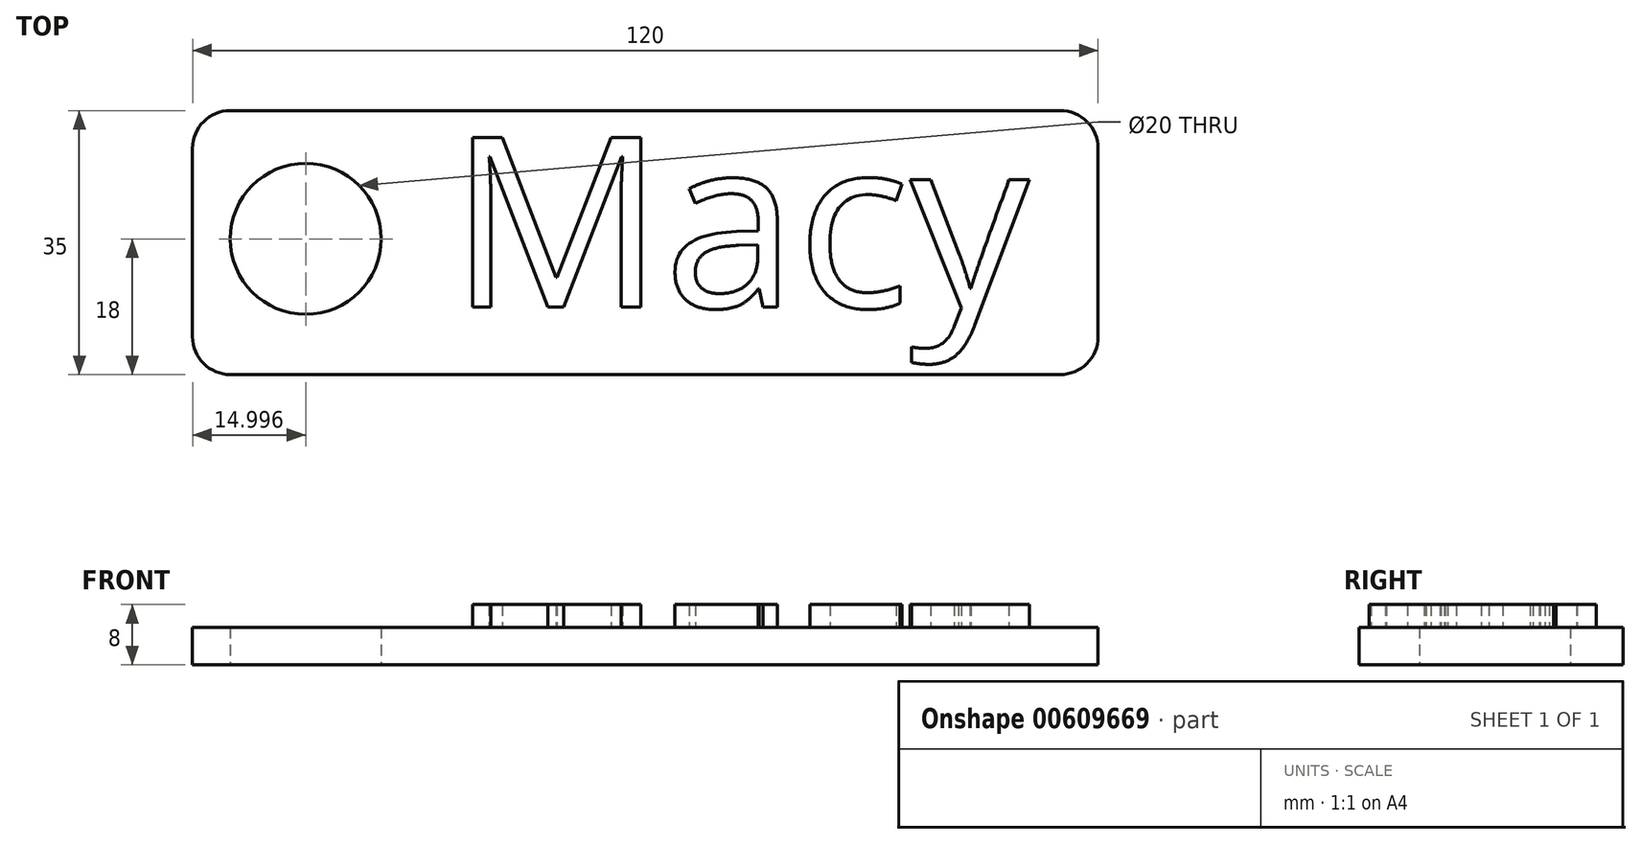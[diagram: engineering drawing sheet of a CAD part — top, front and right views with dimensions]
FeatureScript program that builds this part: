
annotation { "Feature Type Name" : "Feature", "Feature Type Description" : "" }
export const myFeature = defineFeature(function(context is Context, id is Id, definition is map)
    precondition{}
    {
        {
            var Q0;
            Q0=qCreatedBy(makeId("Top.planeOp"),FACE);
            var sketch = newSketch(context, id + "F0", { "sketchPlane" : qUnion([Q0])});
            skLineSegment(sketch, "E0.bottom", {"start": v(59.2, -18) * mm, "end": v(-60.8, -18) * mm});
            skLineSegment(sketch, "E0.top", {"start": v(59.2, 17) * mm, "end": v(-60.8, 17) * mm});
            skLineSegment(sketch, "E0.left", {"start": v(59.2, -18) * mm, "end": v(59.2, 17) * mm});
            skLineSegment(sketch, "E0.right", {"start": v(-60.8, -18) * mm, "end": v(-60.8, 17) * mm});
            skCircle(sketch, "E1", {"center": v(-45.8, 0) * mm, "radius": 10 * mm});
            skSolve(sketch);
        }
        {
            var Q0;
            Q0=makeQuery(id+"F0.imprint","IMPRINT",FACE,{"disambiguationData":[TD([[makeQuery(id+"F0.imprint","IMPRINT",EDGE,{"derivedFrom":sQuery(id+"F0.wireOp",EDGE,"E0.bottom")}),-1.0]])]});
            extrude(context, id + "F1", {"entities" : qUnion([Q0]), "depth" : 5 * mm, "offsetDistance" : 25 * mm});
        }
        {
            var Q0;
            Q0=makeQuery(id+"F1.opExtrude","CAP_FACE",FACE,{"disambiguationData":[OSD([sQuery(id+"F0.wireOp",EDGE,"E0.bottom"),sQuery(id+"F0.wireOp",EDGE,"E0.top"),sQuery(id+"F0.wireOp",EDGE,"E0.left"),sQuery(id+"F0.wireOp",EDGE,"E0.right"),sQuery(id+"F0.wireOp",EDGE,"E1")])],"isStart":false});
            var sketch = newSketch(context, id + "F2", { "sketchPlane" : qUnion([Q0])});
            skText(sketch, "E2", { "text": "Macy", "fontName": "OpenSans-Regular.ttf"});
            const initialGuessF2  = {"E2": [-0.0268, -0.00907, 1, 0, 0.02272]};
            skSetInitialGuess(sketch, initialGuessF2);
            skSolve(sketch);
        }
        {
            var Q0;
            Q0 = qSketchRegion(id + "F2", true);
            extrude(context, id + "F3", {"entities" : qUnion([Q0]), "operationType" : NewBodyOperationType.ADD, "depth" : 3 * mm, "offsetDistance" : 25 * mm});
        }
        {
            var Q0;
            Q0=makeQuery(id+"F1.opExtrude","SWEPT_EDGE",EDGE,{"disambiguationData":[OSD([sQuery(id+"F0.wireOp",EDGE,"E0.bottom"),sQuery(id+"F0.wireOp",EDGE,"E0.left")])]});
            var Q1;
            Q1=makeQuery(id+"F1.opExtrude","SWEPT_EDGE",EDGE,{"disambiguationData":[OSD([sQuery(id+"F0.wireOp",EDGE,"E0.top"),sQuery(id+"F0.wireOp",EDGE,"E0.left")])]});
            var Q2;
            Q2=makeQuery(id+"F1.opExtrude","SWEPT_EDGE",EDGE,{"disambiguationData":[OSD([sQuery(id+"F0.wireOp",EDGE,"E0.bottom"),sQuery(id+"F0.wireOp",EDGE,"E0.right")])]});
            var Q3;
            Q3=makeQuery(id+"F1.opExtrude","SWEPT_EDGE",EDGE,{"disambiguationData":[OSD([sQuery(id+"F0.wireOp",EDGE,"E0.top"),sQuery(id+"F0.wireOp",EDGE,"E0.right")])]});
            fillet(context, id + "F4", {"entities" : qUnion([Q0, Q1, Q2, Q3]), "radius" : 5 * mm, "tangentPropagation" : true, "allowEdgeOverflow" : false});
        }
    });
